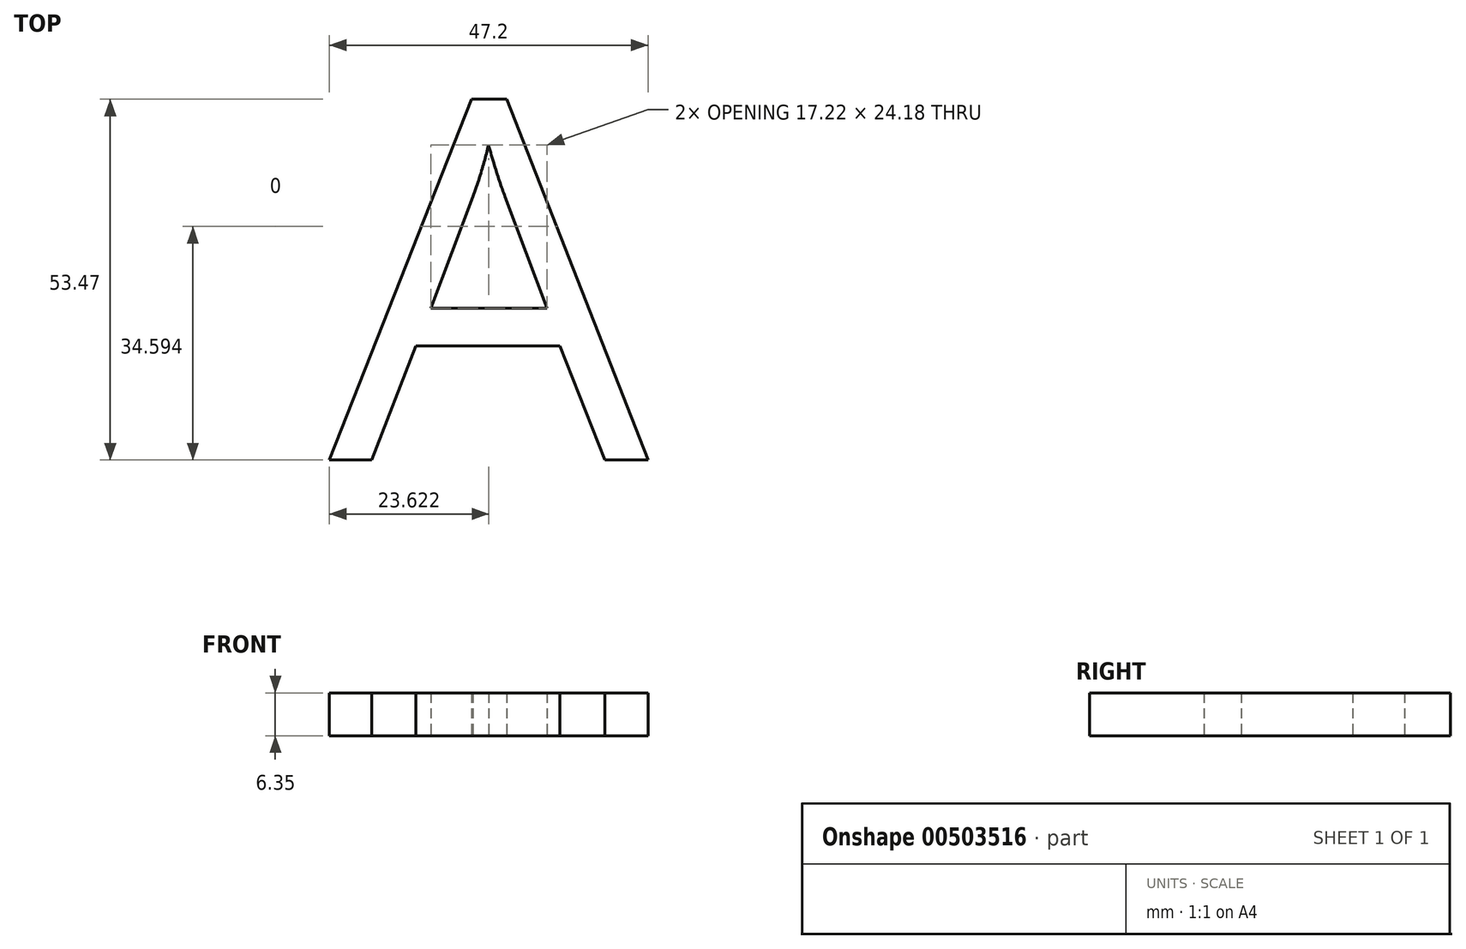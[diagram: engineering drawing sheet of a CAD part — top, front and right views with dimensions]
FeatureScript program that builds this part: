
annotation { "Feature Type Name" : "Feature", "Feature Type Description" : "" }
export const myFeature = defineFeature(function(context is Context, id is Id, definition is map)
    precondition{}
    {
        {
            var Q0;
            Q0=qCreatedBy(makeId("Top.planeOp"),FACE);
            var sketch = newSketch(context, id + "F0", { "sketchPlane" : qUnion([Q0])});
            skText(sketch, "E0", { "text": "A\n", "fontName": "OpenSans-Regular.ttf"});
            const initialGuessF0  = {"E0": [0, 0, 1, 0, 0.0537]};
            skSetInitialGuess(sketch, initialGuessF0);
            skSolve(sketch);
        }
        {
            var Q0;
            Q0 = qSketchRegion(id + "F0", true);
            extrude(context, id + "F1", {"entities" : qUnion([Q0]), "depth" : 6.35 * mm});
        }
    });
